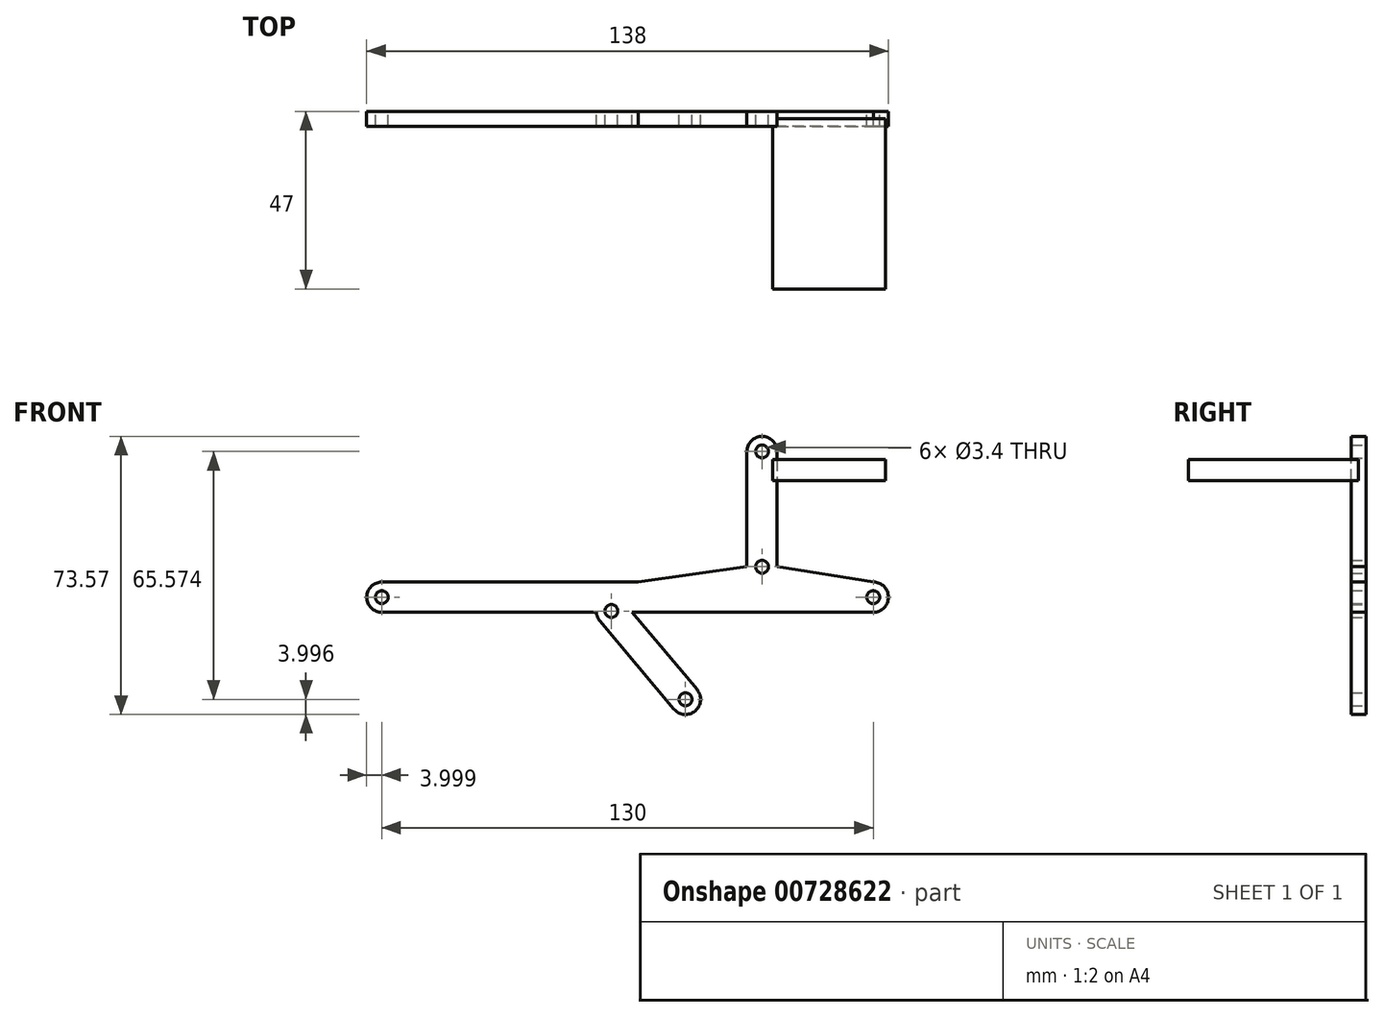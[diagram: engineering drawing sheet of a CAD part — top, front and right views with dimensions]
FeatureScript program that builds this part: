
annotation { "Feature Type Name" : "Feature", "Feature Type Description" : "" }
export const myFeature = defineFeature(function(context is Context, id is Id, definition is map)
    precondition{}
    {
        {
            var Q0;
            Q0=qCreatedBy(makeId("Front.planeOp"),FACE);
            var sketch = newSketch(context, id + "F0", { "sketchPlane" : qUnion([Q0])});
            skLineSegment(sketch, "E0.bottom", {"start": v(-96.28, 40.24) * mm, "end": v(33.72, 40.24) * mm});
            skLineSegment(sketch, "E0.top", {"start": v(-96.28, -40.99) * mm, "end": v(33.72, -40.99) * mm});
            skLineSegment(sketch, "E0.left", {"start": v(-96.28, 40.24) * mm, "end": v(-96.28, -40.99) * mm});
            skLineSegment(sketch, "E0.right", {"start": v(33.72, 40.24) * mm, "end": v(33.72, -40.99) * mm});
            skSolve(sketch);
        }
        {
            var Q0;
            Q0=qCreatedBy(makeId("Front.planeOp"),FACE);
            var sketch = newSketch(context, id + "F1", { "sketchPlane" : qUnion([Q0])});
            skLineSegment(sketch, "E1", {"start": v(0, 0) * mm, "end": v(29.42, -8.05) * mm, "construction": true});
            skCircle(sketch, "E2", {"center": v(0, 0) * mm, "radius": 1.7 * mm});
            skCircle(sketch, "E3", {"center": v(29.42, -8.05) * mm, "radius": 1.7 * mm});
            skCircle(sketch, "E4", {"center": v(0, 30.5) * mm, "radius": 1.7 * mm});
            skLineSegment(sketch, "E5", {"start": v(0, 0) * mm, "end": v(0, 30.5) * mm, "construction": true});
            skCircle(sketch, "E6", {"center": v(-20.25, -35.07) * mm, "radius": 1.7 * mm});
            skLineSegment(sketch, "E7", {"start": v(-20.25, -35.07) * mm, "end": v(0, 0) * mm, "construction": true});
            skCircle(sketch, "E8", {"center": v(-39.86, -11.7) * mm, "radius": 1.7 * mm});
            skLineSegment(sketch, "E9", {"start": v(-39.86, -11.7) * mm, "end": v(-20.25, -35.07) * mm, "construction": true});
            skCircle(sketch, "E10", {"center": v(-100.58, -8.05) * mm, "radius": 1.7 * mm});
            skLineSegment(sketch, "E11", {"start": v(29.42, -8.05) * mm, "end": v(-100.58, -8.05) * mm, "construction": true});
            skCircle(sketch, "E12", {"center": v(-100.58, -8.05) * mm, "radius": 4 * mm});
            skCircle(sketch, "E13", {"center": v(0, 30.5) * mm, "radius": 4 * mm});
            skLineSegment(sketch, "E14", {"start": v(-100.58, -4.05) * mm, "end": v(29.42, -4.05) * mm});
            skLineSegment(sketch, "E15", {"start": v(29.42, -12.05) * mm, "end": v(-100.58, -12.05) * mm});
            skCircle(sketch, "E16", {"center": v(29.42, -8.05) * mm, "radius": 4 * mm});
            skCircle(sketch, "E17", {"center": v(0, 0) * mm, "radius": 4 * mm});
            skCircle(sketch, "E18", {"center": v(-20.25, -35.07) * mm, "radius": 4 * mm});
            skCircle(sketch, "E19", {"center": v(-39.86, -11.7) * mm, "radius": 4 * mm});
            skLineSegment(sketch, "E20", {"start": v(-42.92, -14.28) * mm, "end": v(-23.31, -37.65) * mm});
            skLineSegment(sketch, "E21", {"start": v(-36.8, -9.14) * mm, "end": v(-17.19, -32.5) * mm});
            skLineSegment(sketch, "E22", {"start": v(-48.34, -18.83) * mm, "end": v(-28.33, -2.04) * mm, "construction": true});
            skLineSegment(sketch, "E23", {"start": v(-9.61, 30.5) * mm, "end": v(8.36, 30.5) * mm, "construction": true});
            skLineSegment(sketch, "E24", {"start": v(-4, 30.5) * mm, "end": v(-4, 0) * mm});
            skLineSegment(sketch, "E25", {"start": v(4, 30.5) * mm, "end": v(4, 0) * mm});
            skLineSegment(sketch, "E26", {"start": v(4, 0) * mm, "end": v(29.42, -4.05) * mm});
            skLineSegment(sketch, "E27", {"start": v(-4, 0) * mm, "end": v(-32.8, -4.05) * mm});
            skSolve(sketch);
        }
        {
            var Q0;
            Q0 = qSketchRegion(id + "F1", true);
            extrude(context, id + "F2", {"entities" : qUnion([Q0]), "endBound" : BoundingType.SYMMETRIC, "depth" : 4 * mm, "offsetDistance" : 25 * mm});
        }
        {
            var Q0;
            Q0=qCreatedBy(makeId("Front.planeOp"),FACE);
            var sketch = newSketch(context, id + "F3", { "sketchPlane" : qUnion([Q0])});
            skLineSegment(sketch, "E28.bottom", {"start": v(2.8, 28.36) * mm, "end": v(32.64, 28.36) * mm});
            skLineSegment(sketch, "E28.top", {"start": v(2.8, 22.82) * mm, "end": v(32.64, 22.82) * mm});
            skLineSegment(sketch, "E28.left", {"start": v(2.8, 28.36) * mm, "end": v(2.8, 22.82) * mm});
            skLineSegment(sketch, "E28.right", {"start": v(32.64, 28.36) * mm, "end": v(32.64, 22.82) * mm});
            skSolve(sketch);
        }
        {
            var Q0;
            Q0 = qSketchRegion(id + "F3", true);
            extrude(context, id + "F4", {"entities" : qUnion([Q0]), "operationType" : NewBodyOperationType.ADD, "depth" : 45 * mm, "offsetDistance" : 25 * mm});
        }
    });
